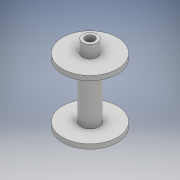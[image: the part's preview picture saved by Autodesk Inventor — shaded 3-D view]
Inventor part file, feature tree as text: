
AUTODESK INVENTOR PART (.ipt)
format: ipt  version: 2017 (Build 210142000, 142)  size: 139,776 bytes
history: native  units: mm
features: sketch x2, revolve x1, extrude x1
ambient origin geometry x8: Origin, YZ Plane, XZ Plane, XY Plane, X Axis, Y Axis, Z Axis, Center Point
bodies: Solid1 (feature_tree)
feature tree (4):
  revolve  "Revolution1"  [1 undecoded]
  extrude  "Extrusion1"  Depth=10.0mm
  sketch  "Sketch1"  dims[d0=2.5mm d1=7.0mm]
  sketch  "Sketch2"  dims[d2=90.0deg d3=4.0mm d4=12.5mm d5=2.5mm d6=2.5mm d7=30.0mm d8=90.0deg d9=15.0mm d10=90.0deg d11=2.5mm d12=10.0mm d13=0.0mm]
note: 1 required parameter value undecoded (feature->parameter linkage not recoverable at this tier; creation-order binding heuristic only, values carry confidence <= 0.55)
